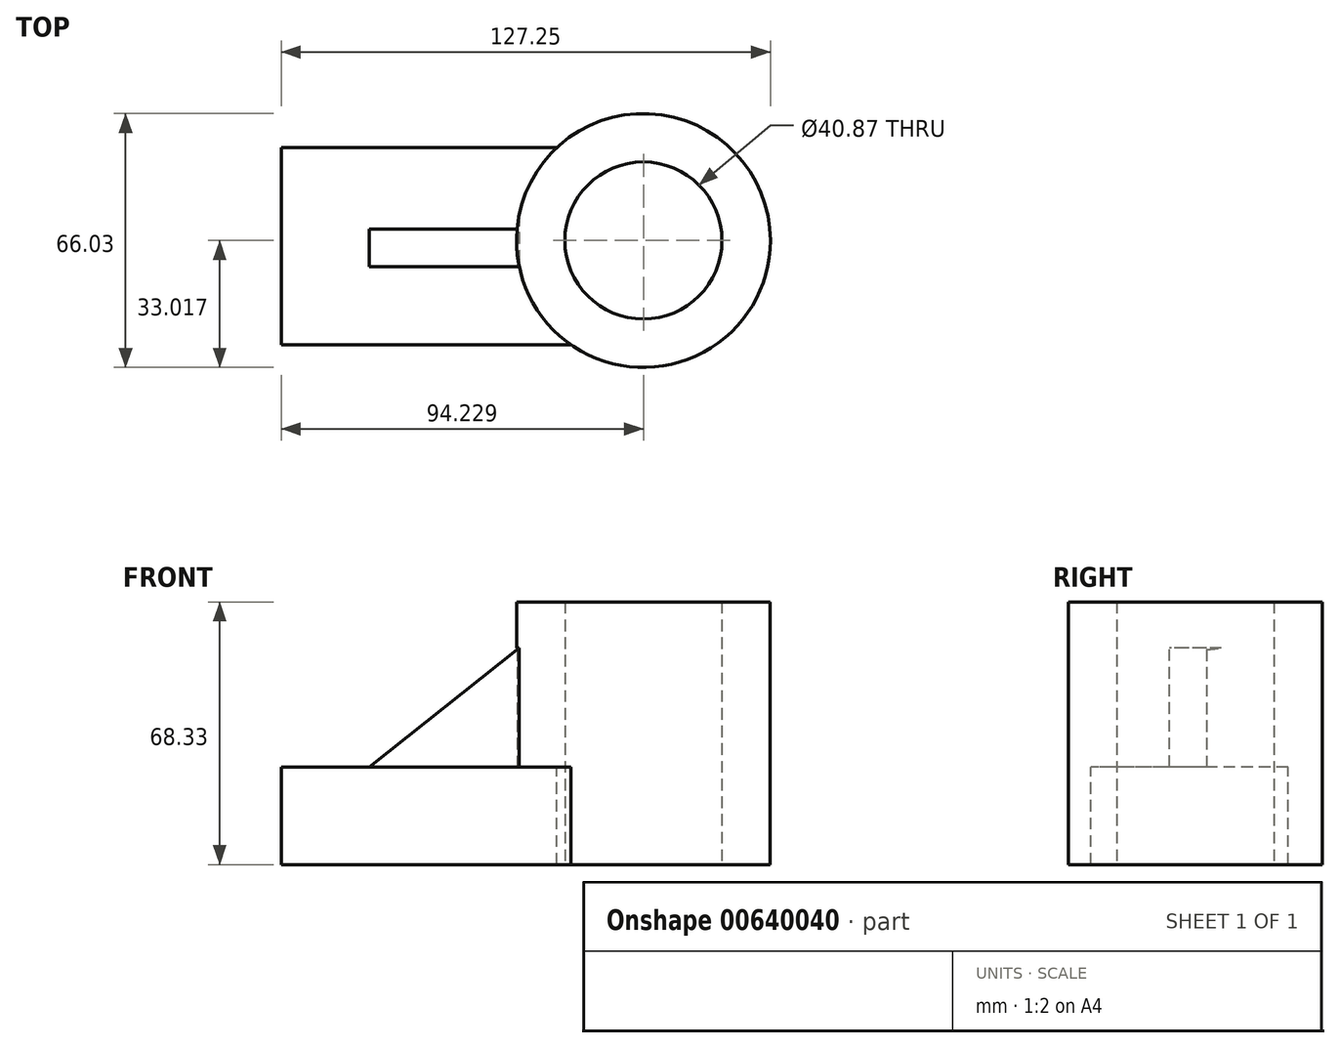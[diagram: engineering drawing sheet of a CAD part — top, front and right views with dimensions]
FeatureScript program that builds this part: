
annotation { "Feature Type Name" : "Feature", "Feature Type Description" : "" }
export const myFeature = defineFeature(function(context is Context, id is Id, definition is map)
    precondition{}
    {
        {
            var Q0;
            Q0=qCreatedBy(makeId("Top.planeOp"),FACE);
            var sketch = newSketch(context, id + "F0", { "sketchPlane" : qUnion([Q0])});
            skLineSegment(sketch, "E0", {"start": v(-47.47, 38.07) * mm, "end": v(-47.47, -13.18) * mm});
            skLineSegment(sketch, "E1", {"start": v(-47.47, -13.18) * mm, "end": v(48.4, -13.18) * mm});
            skLineSegment(sketch, "E2", {"start": v(48.4, -13.18) * mm, "end": v(48.4, 38.07) * mm});
            skLineSegment(sketch, "E3", {"start": v(48.4, 38.07) * mm, "end": v(-47.47, 38.07) * mm});
            skSolve(sketch);
        }
        {
            var Q0;
            Q0 = qSketchRegion(id + "F0", true);
            extrude(context, id + "F1", {"entities" : qUnion([Q0]), "depth" : 25.4 * mm, "offsetDistance" : 25.4 * mm});
        }
        {
            var Q0;
            Q0=makeQuery(id+"F1.opExtrude","CAP_FACE",FACE,{"disambiguationData":[OSD([sQuery(id+"F0.wireOp",EDGE,"E0"),sQuery(id+"F0.wireOp",EDGE,"E1"),sQuery(id+"F0.wireOp",EDGE,"E2"),sQuery(id+"F0.wireOp",EDGE,"E3")])],"isStart":false});
            var sketch = newSketch(context, id + "F2", { "sketchPlane" : qUnion([Q0])});
            skCircle(sketch, "E4", {"center": v(46.76, 13.96) * mm, "radius": 33.02 * mm});
            skCircle(sketch, "E5", {"center": v(46.76, 13.96) * mm, "radius": 20.44 * mm});
            skSolve(sketch);
        }
        {
            var Q0;
            Q0 = qSketchRegion(id + "F2", true);
            extrude(context, id + "F3", {"entities" : qUnion([Q0]), "operationType" : NewBodyOperationType.ADD, "depth" : 42.93 * mm, "offsetDistance" : 25.4 * mm});
        }
        {
            var Q0;
            Q0=makeQuery(id+"F3.opExtrude","CAP_FACE",FACE,{"disambiguationData":[OSD([sQuery(id+"F2.wireOp",EDGE,"E4"),sQuery(id+"F2.wireOp",EDGE,"E5")])],"isStart":true});
            extrude(context, id + "F4", {"entities" : qUnion([Q0]), "operationType" : NewBodyOperationType.ADD, "depth" : 25.4 * mm, "offsetDistance" : 25.4 * mm});
        }
        {
            var Q0;
            {var subQ0=sQuery(id+"F0.wireOp",EDGE,"E2");Q0=makeQuery(id+"F3.boolean.opBoolean","SPLIT",FACE,{"disambiguationData":[TD([makeQuery(id+"F1.opExtrude","SWEPT_FACE",FACE,{"disambiguationData":[OSD([subQ0])]})])],"derivedFrom":makeQuery(id+"F1.opExtrude","CAP_FACE",FACE,{"disambiguationData":[OSD([sQuery(id+"F0.wireOp",EDGE,"E0"),sQuery(id+"F0.wireOp",EDGE,"E1"),subQ0,sQuery(id+"F0.wireOp",EDGE,"E3")])],"isStart":false})});}
            extrude(context, id + "F5", {"entities" : qUnion([Q0]), "operationType" : NewBodyOperationType.REMOVE, "oppositeDirection" : true, "depth" : 26.67 * mm, "offsetDistance" : 25.4 * mm});
        }
        {
            var Q0;
            {var subQ1=sQuery(id+"F0.wireOp",EDGE,"E1");var subQ2=sQuery(id+"F0.wireOp",EDGE,"E3");var subQ3=sQuery(id+"F0.wireOp",EDGE,"E0");Q0=makeQuery(id+"F3.boolean.opBoolean","SPLIT",FACE,{"disambiguationData":[TD([makeQuery(id+"F1.opExtrude","SWEPT_FACE",FACE,{"disambiguationData":[OSD([subQ3])]})])],"derivedFrom":makeQuery(id+"F1.opExtrude","CAP_FACE",FACE,{"disambiguationData":[OSD([subQ3,subQ1,sQuery(id+"F0.wireOp",EDGE,"E2"),subQ2])],"isStart":false})});}
            var sketch = newSketch(context, id + "F6", { "sketchPlane" : qUnion([Q0])});
            skLineSegment(sketch, "E6", {"start": v(-24.56, 7.2) * mm, "end": v(14.44, 7.2) * mm});
            skLineSegment(sketch, "E7", {"start": v(14.44, 7.2) * mm, "end": v(13.87, 16.9) * mm});
            skLineSegment(sketch, "E8", {"start": v(13.87, 16.9) * mm, "end": v(-24.56, 16.9) * mm});
            skLineSegment(sketch, "E9", {"start": v(-24.56, 16.9) * mm, "end": v(-24.56, 7.2) * mm});
            skSolve(sketch);
        }
        {
            var Q0;
            {var subQ0=sQuery(id+"F6.wireOp",EDGE,"E6");Q0=makeQuery(id+"F6.imprint","IMPRINT",FACE,{"disambiguationData":[TD([[makeQuery(id+"F6.imprint","IMPRINT",EDGE,{"derivedFrom":subQ0}),1.0]])]});}
            extrude(context, id + "F7", {"entities" : qUnion([Q0]), "operationType" : NewBodyOperationType.ADD, "depth" : 30.99 * mm, "offsetDistance" : 25.4 * mm});
        }
        {
            var Q0;
            Q0=makeQuery(id+"F7.opExtrude","SWEPT_FACE",FACE,{"disambiguationData":[OSD([sQuery(id+"F6.wireOp",EDGE,"E6")])]});
            var sketch = newSketch(context, id + "F8", { "sketchPlane" : qUnion([Q0])});
            skLineSegment(sketch, "E10", {"start": v(-24.56, 25.4) * mm, "end": v(14.44, 56.39) * mm});
            skSolve(sketch);
        }
        {
            var Q0;
            Q0=makeQuery(id+"F8.imprint","IMPRINT",FACE,{"disambiguationData":[TD([[makeQuery(id+"F8.imprint","IMPRINT",EDGE,{"derivedFrom":sQuery(id+"F8.wireOp",EDGE,"E10")}),1.0]])]});
            extrude(context, id + "F9", {"entities" : qUnion([Q0]), "operationType" : NewBodyOperationType.REMOVE, "oppositeDirection" : true, "depth" : 69.6 * mm, "offsetDistance" : 25.4 * mm});
        }
    });
